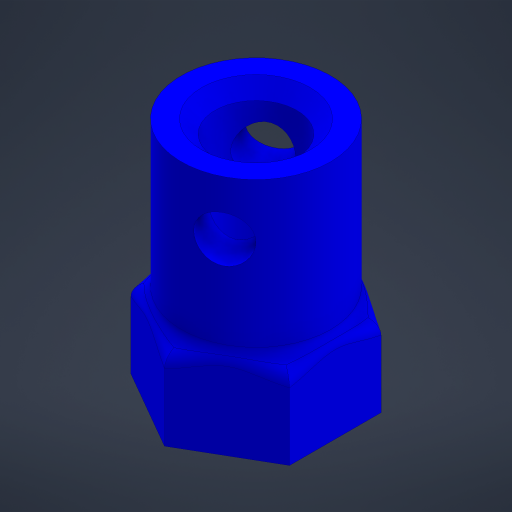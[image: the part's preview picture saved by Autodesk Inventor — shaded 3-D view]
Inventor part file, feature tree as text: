
AUTODESK INVENTOR PART (.ipt)
format: ipt  version: 2024 (Build 280153000, 153)  size: 307,200 bytes
history: native  units: mm
features: extrude x3, sketch x3, other x1, chamfer x1, fillet x1
ambient origin geometry x8: Origin, YZ Plane, XZ Plane, XY Plane, X Axis, Y Axis, Z Axis, Center Point
bodies: Body1 (feature_tree)
feature tree (9):
  other  "Твердое тело1"
  extrude  "Выдавливание1"  Depth=6.2mm
  extrude  "Выдавливание2"  Depth=11.3mm
  chamfer  "Фаска1"  Distance=12.0mm
  fillet  "Сопряжение1"  Radius=12.0mm
  extrude  "Выдавливание3"  Depth=4.0mm
  sketch  "Эскиз1"
  sketch  "Эскиз2"
  sketch  "Эскиз3"
